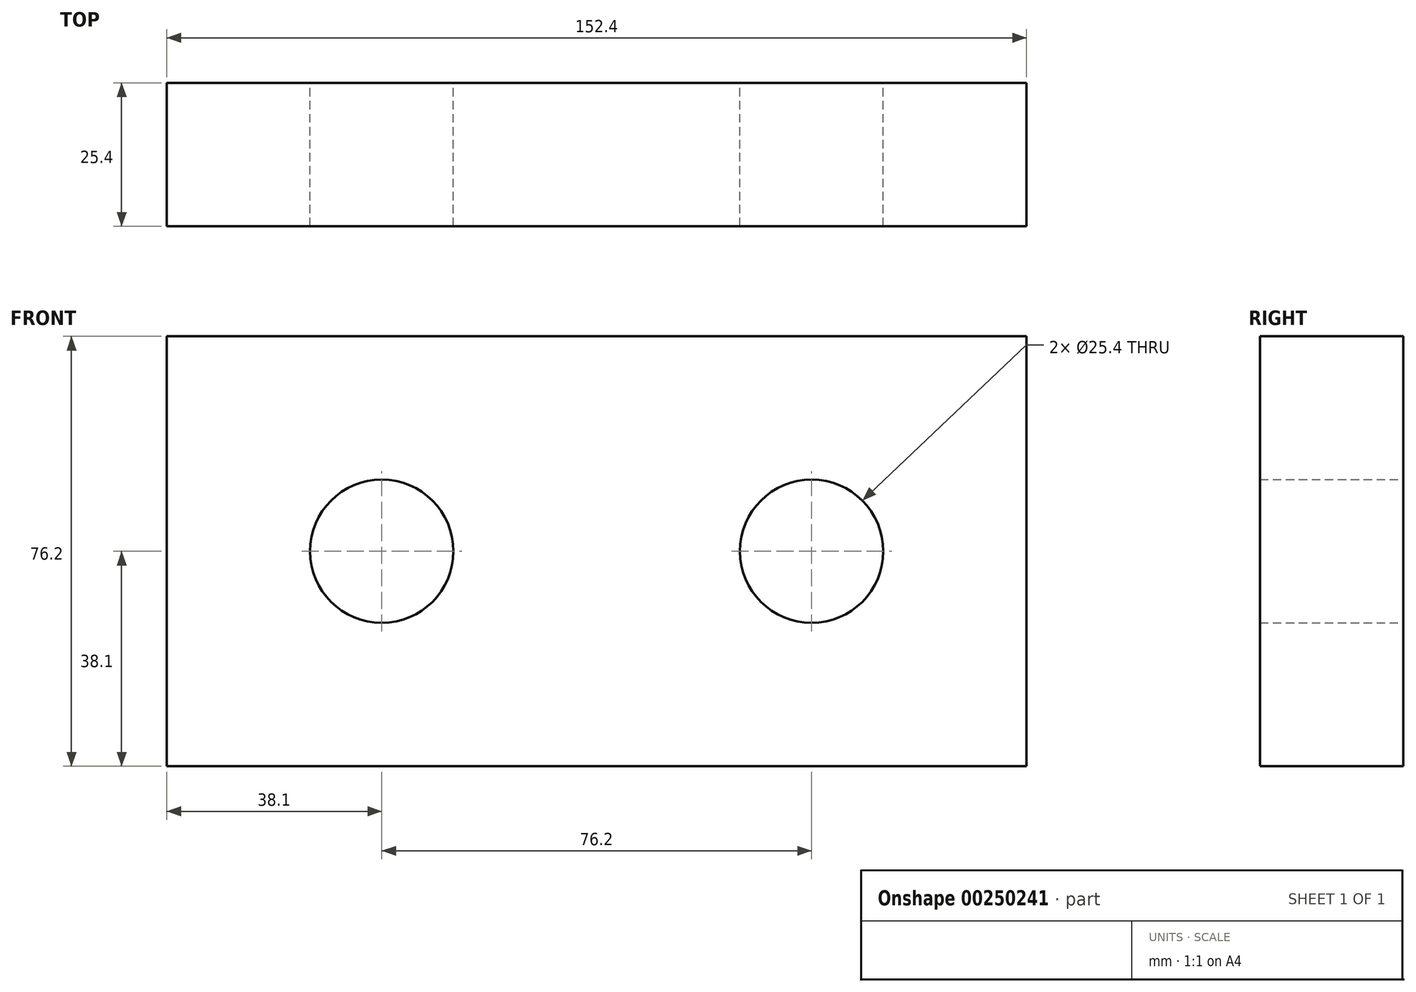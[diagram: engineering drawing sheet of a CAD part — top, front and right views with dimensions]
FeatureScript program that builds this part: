
annotation { "Feature Type Name" : "Feature", "Feature Type Description" : "" }
export const myFeature = defineFeature(function(context is Context, id is Id, definition is map)
    precondition{}
    {
        {
            var Q0;
            Q0=qCreatedBy(makeId("Front.planeOp"),FACE);
            var sketch = newSketch(context, id + "F0", { "sketchPlane" : qUnion([Q0])});
            skLineSegment(sketch, "E0.bottom", {"start": v(76.2, 38.1) * mm, "end": v(-76.2, 38.1) * mm});
            skLineSegment(sketch, "E0.top", {"start": v(76.2, -38.1) * mm, "end": v(-76.2, -38.1) * mm});
            skLineSegment(sketch, "E0.left", {"start": v(76.2, 38.1) * mm, "end": v(76.2, -38.1) * mm});
            skLineSegment(sketch, "E0.right", {"start": v(-76.2, 38.1) * mm, "end": v(-76.2, -38.1) * mm});
            skPoint(sketch, "E0.middle", {"position": v(0, 0) * mm});
            skLineSegment(sketch, "E1", {"start": v(0, 0) * mm, "end": v(-38.1, 0) * mm});
            skCircle(sketch, "E2", {"center": v(-38.1, 0) * mm, "radius": 12.7 * mm});
            skLineSegment(sketch, "E3", {"start": v(0, 0) * mm, "end": v(38.1, 0) * mm});
            skCircle(sketch, "E4", {"center": v(38.1, 0) * mm, "radius": 12.7 * mm});
            skSolve(sketch);
        }
        {
            var Q0;
            Q0=makeQuery(id+"F0.imprint","IMPRINT",FACE,{"disambiguationData":[TD([[makeQuery(id+"F0.imprint","IMPRINT",EDGE,{"derivedFrom":sQuery(id+"F0.wireOp",EDGE,"E0.bottom")}),1.0]])]});
            extrude(context, id + "F1", {"entities" : qUnion([Q0]), "depth" : 25.4 * mm});
        }
    });
